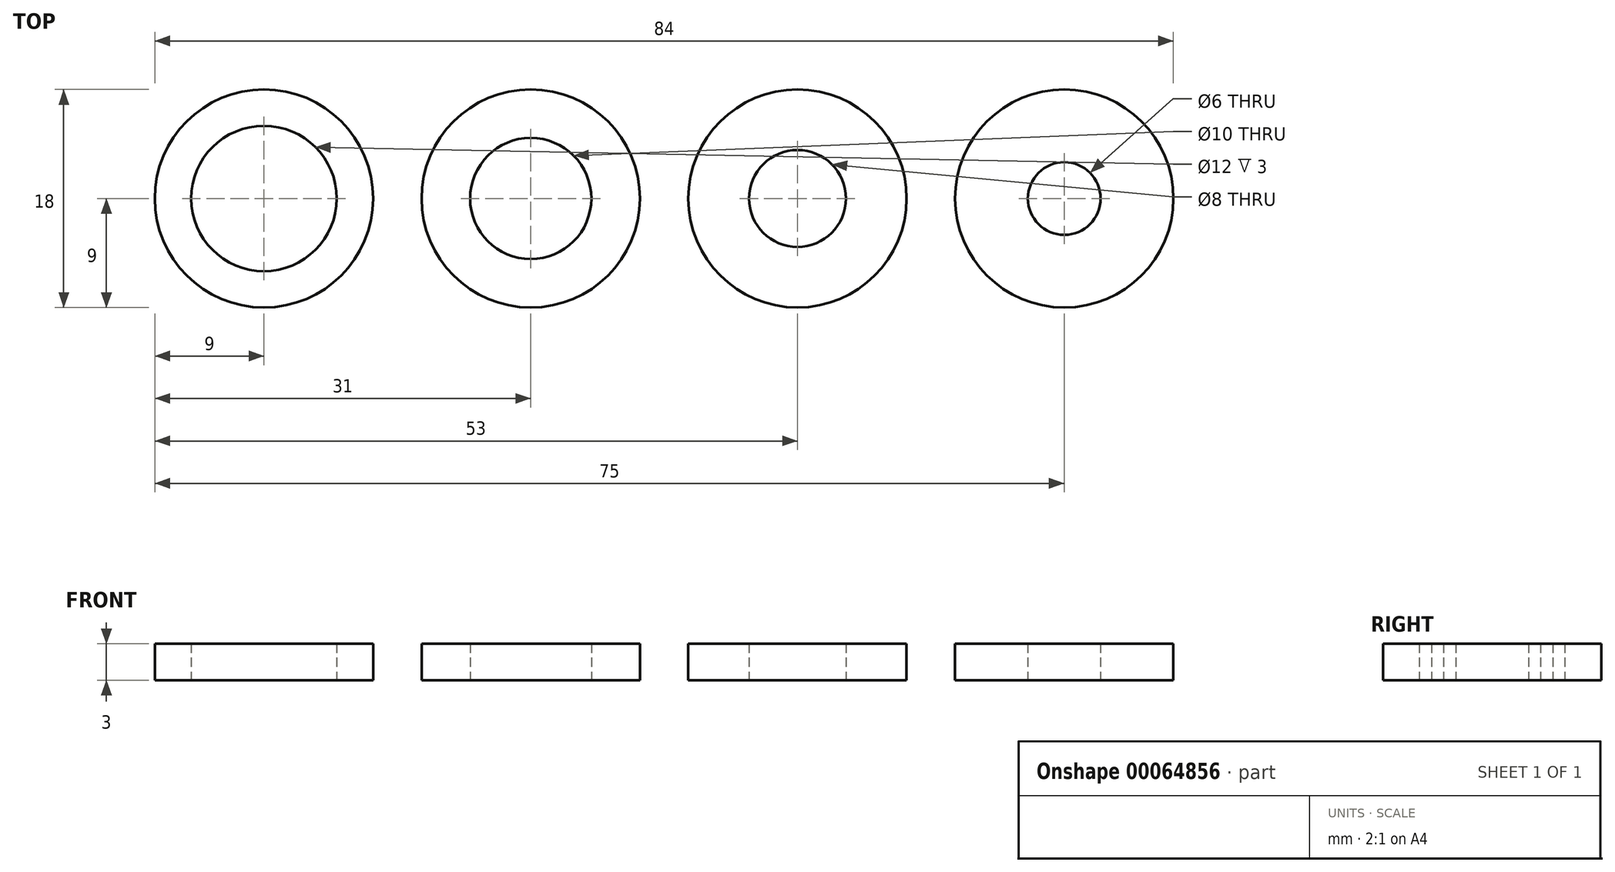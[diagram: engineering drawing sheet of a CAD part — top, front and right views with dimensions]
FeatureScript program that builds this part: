
annotation { "Feature Type Name" : "Feature", "Feature Type Description" : "" }
export const myFeature = defineFeature(function(context is Context, id is Id, definition is map)
    precondition{}
    {
        {
            var Q0;
            Q0=qCreatedBy(makeId("Top.planeOp"),FACE);
            var sketch = newSketch(context, id + "F0", { "sketchPlane" : qUnion([Q0])});
            skCircle(sketch, "E0", {"center": v(0, 0) * mm, "radius": 9 * mm});
            skCircle(sketch, "E1", {"center": v(22, 0) * mm, "radius": 9 * mm});
            skCircle(sketch, "E2", {"center": v(44, 0) * mm, "radius": 9 * mm});
            skCircle(sketch, "E3", {"center": v(66, 0) * mm, "radius": 9 * mm});
            skLineSegment(sketch, "E4", {"start": v(0, 0) * mm, "end": v(22, 0) * mm, "construction": true});
            skLineSegment(sketch, "E5", {"start": v(22, 0) * mm, "end": v(44, 0) * mm, "construction": true});
            skLineSegment(sketch, "E6", {"start": v(44, 0) * mm, "end": v(66, 0) * mm, "construction": true});
            skCircle(sketch, "E7", {"center": v(0, 0) * mm, "radius": 6 * mm});
            skCircle(sketch, "E8", {"center": v(22, 0) * mm, "radius": 5 * mm});
            skCircle(sketch, "E9", {"center": v(44, 0) * mm, "radius": 4 * mm});
            skCircle(sketch, "E10", {"center": v(66, 0) * mm, "radius": 3 * mm});
            skSolve(sketch);
        }
        {
            var Q0;
            Q0 = qSketchRegion(id + "F0", true);
            extrude(context, id + "F1", {"entities" : qUnion([Q0]), "depth" : 3 * mm});
        }
    });
